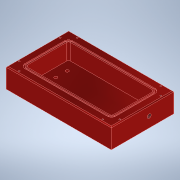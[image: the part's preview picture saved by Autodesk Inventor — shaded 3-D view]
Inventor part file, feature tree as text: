
AUTODESK INVENTOR PART (.ipt)
format: ipt  version: 2022 (Build 260153000, 153)  size: 222,208 bytes
history: native  units: mm
features: sketch x6, extrude x3, hole x3, fillet x1, chamfer x1
ambient origin geometry x8: Origin, YZ Plane, XZ Plane, XY Plane, X Axis, Y Axis, Z Axis, Center Point
bodies: Volumenkörper1 (feature_tree)
feature tree (14):
  extrude  "Extrusion1"  Depth=139.7mm
  extrude  "Extrusion2"  Depth=192.0mm
  fillet  "Rundung1"  Radius=96.0mm
  chamfer  "Fase1"  Distance=36.0mm
  sketch  "Skizze4"  dims[d10=4.0mm d11=2.0mm d12=2.0mm d13=45.0deg]
  hole  "Bohrung7"  [1 undecoded]
  hole  "Hole9"  [1 undecoded]
  hole  "Hole10"  [1 undecoded]
  extrude  "Extrusion5"  Depth=1.905mm
  sketch  "Skizze1"  dims[d0=234.95mm d2=139.7mm]
  sketch  "Skizze2"  dims[d3=44.45mm d4=0.0mm d5=192.0mm d7=96.0mm d8=36.0mm d9=0.0mm]
  sketch  "Sketch12"  dims[d153=24.0mm d154=24.0mm]
  sketch  "Sketch13"  dims[d155=5.0mm d156=5.0mm]
  sketch  "Sketch14"  dims[d157=24.0mm d158=5.0mm d159=5.0mm d160=24.0mm d161=24.0mm d162=5.0mm d163=5.0mm d164=24.0mm d165=5.0mm d166=24.0mm d167=5.0mm d168=24.0mm d169=3.242mm d170=6.0mm d171=8.0mm d172=4.6mm d173=14.3117mm d174=20.0mm d175=20.594885mm d193=76.2mm d194=76.2mm d195=6.756mm d196=6.924mm d197=12.878mm d198=2.0mm d199=14.3117mm d200=8.0mm d201=20.594885mm d202=25.4mm d203=25.4mm d204=25.4mm d205=25.4mm d206=55.0mm d207=23.0mm d208=7.95mm d209=6.924mm d210=0.624793mm d211=8.304mm d212=12.878mm d213=2.0mm d214=14.3117mm d215=11.628mm d216=20.594885mm d220=2.54mm d221=2.54mm d222=2.54mm d225=3.175mm d226=3.175mm d227=1.905mm d228=0.0mm]
note: 3 required parameter values undecoded (feature->parameter linkage not recoverable at this tier; creation-order binding heuristic only, values carry confidence <= 0.55)
